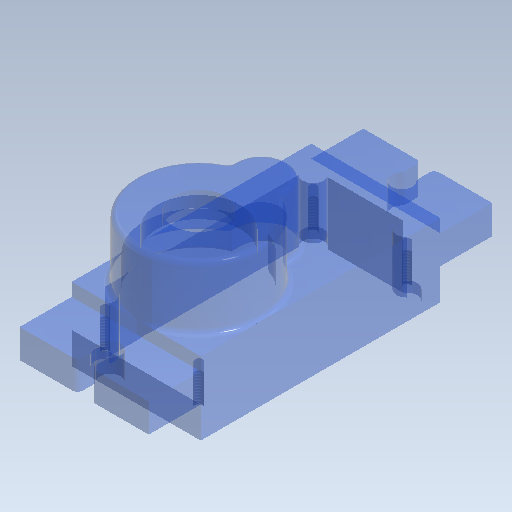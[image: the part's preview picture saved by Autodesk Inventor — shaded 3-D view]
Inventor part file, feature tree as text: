
AUTODESK INVENTOR PART (.ipt)
format: ipt  version: 2020 (Build 240168000, 168)  size: 347,136 bytes
history: native  units: mm
features: sketch x10, extrude x9, projected_geometry x8, other x1, hole x1, chamfer x1, mirror x1, fillet x1
ambient origin geometry x8: Origin, YZ Plane, XZ Plane, XY Plane, X Axis, Y Axis, Z Axis, Center Point
bodies: Body1 (feature_tree)
feature tree (32):
  other  "Твердое тело1"
  extrude  "Выдавливание1"  Depth=12.4mm
  extrude  "Выдавливание2"  Depth=23.0mm
  extrude  "Выдавливание3"  Depth=7.0mm TaperAngle=0.0deg
  hole  "Отверстие1"  [1 undecoded]
  chamfer  "Фаска1"  Distance=6.0mm
  extrude  "Выдавливание4"  Depth=9.0mm
  extrude  "Выдавливание5"  Depth=20.0mm
  extrude  "Выдавливание6"  Depth=2.0mm
  extrude  "Выдавливание7"  Depth=5.0mm TaperAngle=0.0deg
  extrude  "Выдавливание8"  Depth=0.2mm TaperAngle=45.0deg
  extrude  "Выдавливание9"  Depth=12.0mm
  mirror  "Зеркальное отражение1"
  fillet  "Сопряжение1"  Radius=5.0mm
  sketch  "Эскиз1"
  sketch  "Эскиз2"
  projected_geometry  "Спроецированная петля1"
  sketch  "Эскиз3"
  sketch  "Эскиз4"
  projected_geometry  "Спроецированная петля2"
  projected_geometry  "Спроецированная петля3"
  projected_geometry  "Спроецированная петля4"
  projected_geometry  "Спроецированная петля5"
  sketch  "Эскиз5"
  sketch  "Эскиз6"
  projected_geometry  "Спроецированная петля6"
  sketch  "Эскиз7"
  projected_geometry  "Спроецированная петля7"
  sketch  "Эскиз8"
  projected_geometry  "Спроецированная петля8"
  sketch  "Эскиз9"
  sketch  "Эскиз10"
note: 1 required parameter value undecoded (feature->parameter linkage not recoverable at this tier; creation-order binding heuristic only, values carry confidence <= 0.55)
